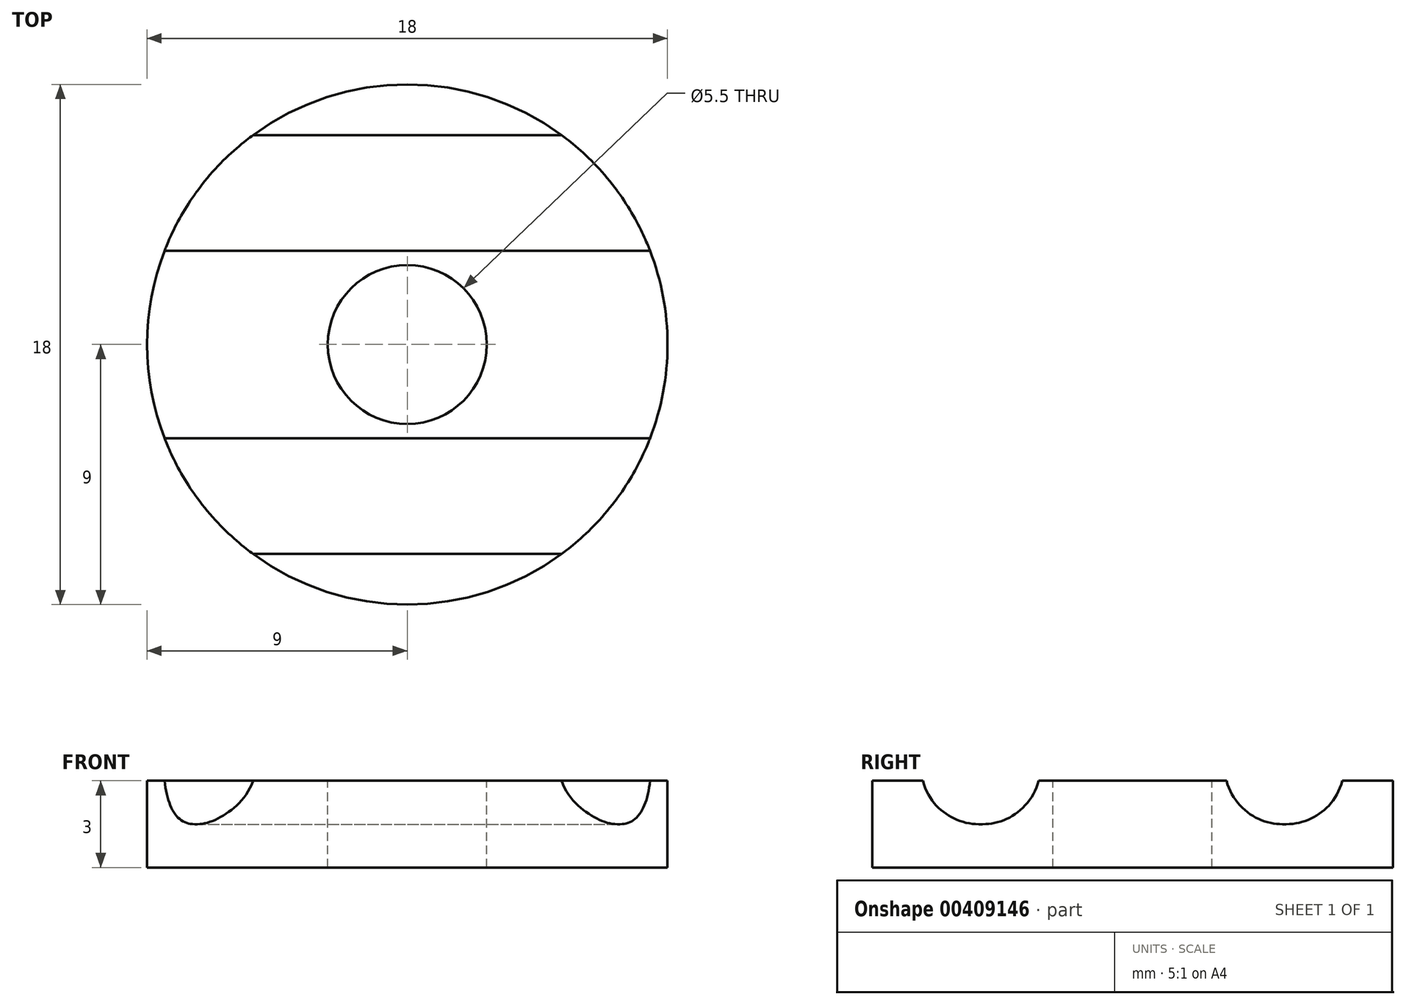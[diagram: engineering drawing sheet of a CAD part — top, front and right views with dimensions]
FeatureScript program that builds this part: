
annotation { "Feature Type Name" : "Feature", "Feature Type Description" : "" }
export const myFeature = defineFeature(function(context is Context, id is Id, definition is map)
    precondition{}
    {
        {
            var Q0;
            Q0=qCreatedBy(makeId("Top.planeOp"),FACE);
            var sketch = newSketch(context, id + "F0", { "sketchPlane" : qUnion([Q0])});
            skCircle(sketch, "E0", {"center": v(0, 0) * mm, "radius": 9 * mm});
            skCircle(sketch, "E1", {"center": v(0, 0) * mm, "radius": 2.75 * mm});
            skLineSegment(sketch, "E2", {"start": v(-5.33, -7.25) * mm, "end": v(5.33, -7.25) * mm});
            skLineSegment(sketch, "E3", {"start": v(-8.4, -3.25) * mm, "end": v(8.4, -3.25) * mm});
            skLineSegment(sketch, "E4.MirrorCS", {"start": v(-8.4, 3.25) * mm, "end": v(8.4, 3.25) * mm});
            skLineSegment(sketch, "E5.MirrorCS", {"start": v(-5.33, 7.25) * mm, "end": v(5.33, 7.25) * mm});
            skSolve(sketch);
        }
        {
            var Q0;
            {var subQ0=sQuery(id+"F0.wireOp",EDGE,"E5.MirrorCS");Q0=makeQuery(id+"F0.imprint","IMPRINT",FACE,{"disambiguationData":[TD([[makeQuery(id+"F0.imprint","IMPRINT",EDGE,{"derivedFrom":subQ0}),1.0]])]});}
            var Q1;
            {var subQ0=sQuery(id+"F0.wireOp",EDGE,"E4.MirrorCS");Q1=makeQuery(id+"F0.imprint","IMPRINT",FACE,{"disambiguationData":[TD([[makeQuery(id+"F0.imprint","IMPRINT",EDGE,{"derivedFrom":subQ0}),1.0]])]});}
            var Q2;
            {var subQ0=sQuery(id+"F0.wireOp",EDGE,"E2");Q2=makeQuery(id+"F0.imprint","IMPRINT",FACE,{"disambiguationData":[TD([[makeQuery(id+"F0.imprint","IMPRINT",EDGE,{"derivedFrom":subQ0}),1.0]])]});}
            var Q3;
            {var subQ0=sQuery(id+"F0.wireOp",EDGE,"E2");Q3=makeQuery(id+"F0.imprint","IMPRINT",FACE,{"disambiguationData":[TD([[makeQuery(id+"F0.imprint","IMPRINT",EDGE,{"derivedFrom":subQ0}),-1.0]])]});}
            var Q4;
            Q4=makeQuery(id+"F0.imprint","IMPRINT",FACE,{"disambiguationData":[TD([[makeQuery(id+"F0.imprint","IMPRINT",EDGE,{"derivedFrom":sQuery(id+"F0.wireOp",EDGE,"E1")}),-1.0]])]});
            extrude(context, id + "F1", {"entities" : qUnion([Q0, Q1, Q2, Q3, Q4]), "oppositeDirection" : true, "depth" : 3 * mm, "offsetDistance" : 25 * mm});
        }
        {
            var Q0;
            {var subQ0=sQuery(id+"F0.wireOp",EDGE,"E4.MirrorCS");Q0=makeQuery(id+"F0.imprint","IMPRINT",FACE,{"disambiguationData":[TD([[makeQuery(id+"F0.imprint","IMPRINT",EDGE,{"derivedFrom":subQ0}),1.0]])]});}
            var Q1;
            {var subQ0=sQuery(id+"F0.wireOp",EDGE,"E2");Q1=makeQuery(id+"F0.imprint","IMPRINT",FACE,{"disambiguationData":[TD([[makeQuery(id+"F0.imprint","IMPRINT",EDGE,{"derivedFrom":subQ0}),1.0]])]});}
            extrude(context, id + "F2", {"entities" : qUnion([Q0, Q1]), "operationType" : NewBodyOperationType.REMOVE, "oppositeDirection" : true, "depth" : 1.5 * mm, "offsetDistance" : 25 * mm});
        }
        {
            var Q0;
            Q0=makeQuery(id+"F2.boolean.opBoolean","COPY",EDGE,{"derivedFrom":makeQuery(id+"F2.opExtrude","CAP_EDGE",EDGE,{"disambiguationData":[OSD([sQuery(id+"F0.wireOp",EDGE,"E4.MirrorCS")])],"isStart":false})});
            var Q1;
            Q1=makeQuery(id+"F2.boolean.opBoolean","COPY",EDGE,{"derivedFrom":makeQuery(id+"F2.opExtrude","CAP_EDGE",EDGE,{"disambiguationData":[OSD([sQuery(id+"F0.wireOp",EDGE,"E5.MirrorCS")])],"isStart":false})});
            var Q2;
            Q2=makeQuery(id+"F2.boolean.opBoolean","COPY",EDGE,{"derivedFrom":makeQuery(id+"F2.opExtrude","CAP_EDGE",EDGE,{"disambiguationData":[OSD([sQuery(id+"F0.wireOp",EDGE,"E3")])],"isStart":false})});
            var Q3;
            Q3=makeQuery(id+"F2.boolean.opBoolean","COPY",EDGE,{"derivedFrom":makeQuery(id+"F2.opExtrude","CAP_EDGE",EDGE,{"disambiguationData":[OSD([sQuery(id+"F0.wireOp",EDGE,"E2")])],"isStart":false})});
            fillet(context, id + "F3", {"entities" : qUnion([Q0, Q1, Q2, Q3]), "radius" : 2 * mm, "tangentPropagation" : true, "allowEdgeOverflow" : false});
        }
    });
